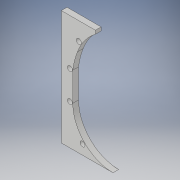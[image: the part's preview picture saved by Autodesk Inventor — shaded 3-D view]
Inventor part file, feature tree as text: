
AUTODESK INVENTOR PART (.ipt)
format: ipt  version: 2018 (Build 220112000, 112)  size: 173,568 bytes
history: native  units: in
note: dims shown in document units (in); Inventor stores cm internally (conversion verified against a paired STEP export)
features: extrude x1, sketch x1
ambient origin geometry x8: Origin, YZ Plane, XZ Plane, XY Plane, X Axis, Y Axis, Z Axis, Center Point
bodies: Body1 (feature_tree)
feature tree (2):
  extrude  "Extrusion2"  Depth=5.9332in
  sketch  "Sketch1"  dims[d0=24.0in d1=8.25in d2=12.0in d3=6.5in d4=6.5in d5=12.0in d6=7.0in d7=7.0in d8=1.0in d9=0.5in d10=135.0deg d11=6.5in d12=135.0deg d13=6.5in d14=5.0in d15=0.625in d16=1.0in d17=5.0in d18=0.625in d19=1.0in d20=5.0in d21=3.0in d22=6.0in d23=1.0in d24=2.0in d25=5.0in d26=0.8727in d33=6.25in d34=0.8727in d35=1.0994in d36=6.25in d37=180.0deg d45=150.0deg d46=6.25in d47=180.0deg d48=0.5in d49=0.5in d50=0.5in d52=0.5in d53=1.0in d55=8.4437in d56=0.875in d57=0.875in d58=0.875in d59=0.875in d60=5.3033in d72=26.0in d73=20.0in d74=90.0deg d75=1.0in d76=0.0in d77=5.9332in d78=0.6126in]
